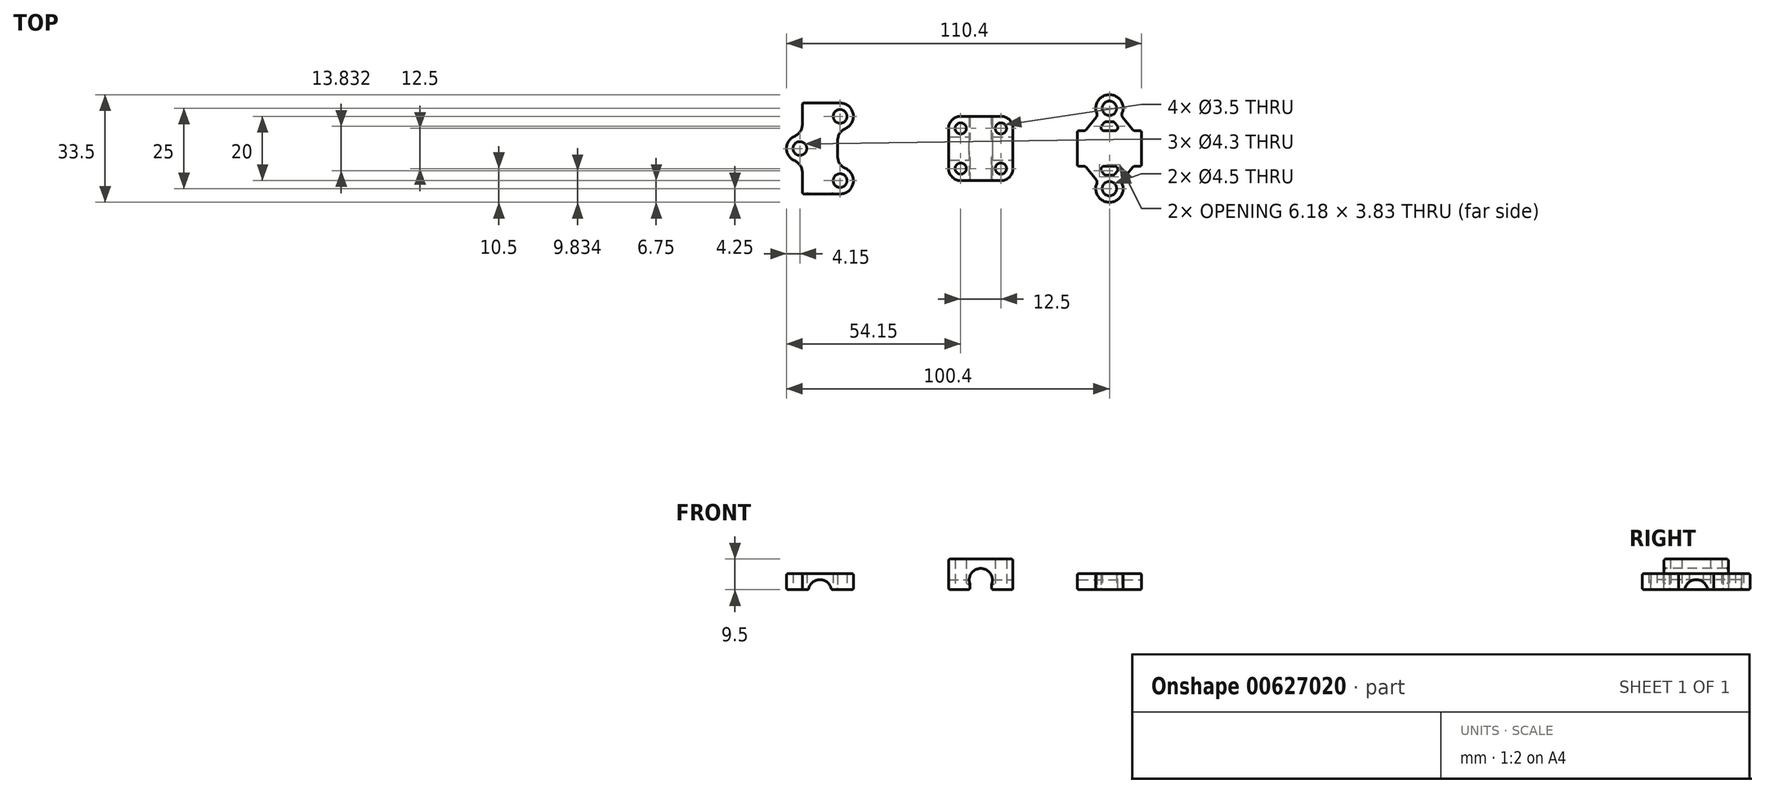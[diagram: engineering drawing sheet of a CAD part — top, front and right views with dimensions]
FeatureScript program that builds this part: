
annotation { "Feature Type Name" : "Feature", "Feature Type Description" : "" }
export const myFeature = defineFeature(function(context is Context, id is Id, definition is map)
    precondition{}
    {
        {
            var Q0;
            Q0=qCreatedBy(makeId("Top.planeOp"),FACE);
            var sketch = newSketch(context, id + "F0", { "sketchPlane" : qUnion([Q0])});
            skLineSegment(sketch, "E0", {"start": v(3.5, 3.7) * mm, "end": v(3.5, 0) * mm, "construction": true});
            skCircle(sketch, "E1", {"center": v(6.25, 6.25) * mm, "radius": 1.75 * mm});
            skLineSegment(sketch, "E2", {"start": v(8.8, 3.5) * mm, "end": v(0, 3.5) * mm, "construction": true});
            skArc(sketch, "E3", {"start": v(10, 6.25) * mm, "mid": v(8.9, 8.9) * mm, "end": v(6.25, 10) * mm});
            skLineSegment(sketch, "E4", {"start": v(6.25, 10) * mm, "end": v(0, 10) * mm});
            skLineSegment(sketch, "E5", {"start": v(10, 6.25) * mm, "end": v(10, 0) * mm});
            skLineSegment(sketch, "E6.MirrorCS", {"start": v(-6.25, 10) * mm, "end": v(0, 10) * mm});
            skArc(sketch, "E7.MirrorCS", {"start": v(-10, 6.25) * mm, "mid": v(-8.9, 8.9) * mm, "end": v(-6.25, 10) * mm});
            skLineSegment(sketch, "E8.MirrorCS", {"start": v(-10, 6.25) * mm, "end": v(-10, 0) * mm});
            skCircle(sketch, "E9.MirrorC", {"center": v(-6.25, 6.25) * mm, "radius": 1.75 * mm});
            skLineSegment(sketch, "E10.MirrorCS", {"start": v(-10, -6.25) * mm, "end": v(-10, 0) * mm});
            skArc(sketch, "E11.MirrorCS", {"start": v(-10, -6.25) * mm, "mid": v(-8.9, -8.9) * mm, "end": v(-6.25, -10) * mm});
            skCircle(sketch, "E12.MirrorC", {"center": v(-6.25, -6.25) * mm, "radius": 1.75 * mm});
            skLineSegment(sketch, "E13.MirrorCS", {"start": v(-6.25, -10) * mm, "end": v(0, -10) * mm});
            skLineSegment(sketch, "E14.MirrorCS", {"start": v(6.25, -10) * mm, "end": v(0, -10) * mm});
            skArc(sketch, "E15.MirrorCS", {"start": v(10, -6.25) * mm, "mid": v(8.9, -8.9) * mm, "end": v(6.25, -10) * mm});
            skCircle(sketch, "E16.MirrorC", {"center": v(6.25, -6.25) * mm, "radius": 1.75 * mm});
            skLineSegment(sketch, "E17.MirrorCS", {"start": v(10, -6.25) * mm, "end": v(10, 0) * mm});
            skSolve(sketch);
        }
        {
            var Q0;
            Q0 = qSketchRegion(id + "F0", true);
            extrude(context, id + "F1", {"entities" : qUnion([Q0]), "depth" : 10 * mm, "offsetDistance" : 25 * mm, "hasSecondDirection" : true, "secondDirectionOppositeDirection" : true, "secondDirectionDepth" : -0.5 * mm});
        }
        {
            var Q0;
            Q0=qCreatedBy(makeId("Front.planeOp"),FACE);
            var sketch = newSketch(context, id + "F2", { "sketchPlane" : qUnion([Q0])});
            skArc(sketch, "E18", {"start": v(3.4, 2.32) * mm, "mid": v(0, 7.1) * mm, "end": v(-3.4, 2.32) * mm});
            skLineSegment(sketch, "E19", {"start": v(-3.4, 2.32) * mm, "end": v(-3.4, 0) * mm});
            skLineSegment(sketch, "E20", {"start": v(-3.4, 0) * mm, "end": v(3.4, 0) * mm});
            skLineSegment(sketch, "E21.MirrorCS", {"start": v(3.4, 2.32) * mm, "end": v(3.4, 0) * mm});
            skSolve(sketch);
        }
        {
            var Q0;
            Q0 = qSketchRegion(id + "F2", true);
            extrude(context, id + "F3", {"entities" : qUnion([Q0]), "operationType" : NewBodyOperationType.REMOVE, "endBound" : BoundingType.SYMMETRIC, "oppositeDirection" : true, "depth" : 25 * mm, "offsetDistance" : 25 * mm});
        }
        {
            var Q0;
            Q0=makeQuery(id+"F3.boolean.opBoolean","INTERSECT",EDGE,{"derivedFrom":[makeQuery(id+"F1.opExtrude","SWEPT_FACE",FACE,{"disambiguationData":[OSD([sQuery(id+"F0.wireOp",EDGE,"E4"),sQuery(id+"F0.wireOp",EDGE,"E6.MirrorCS")])]}),makeQuery(id+"F3.opExtrude","SWEPT_FACE",FACE,{"disambiguationData":[OSD([sQuery(id+"F2.wireOp",EDGE,"E18")])]})]});
            var Q1;
            Q1=makeQuery(id+"F3.boolean.opBoolean","INTERSECT",EDGE,{"derivedFrom":[makeQuery(id+"F1.opExtrude","SWEPT_FACE",FACE,{"disambiguationData":[OSD([sQuery(id+"F0.wireOp",EDGE,"E4"),sQuery(id+"F0.wireOp",EDGE,"E6.MirrorCS")])]}),makeQuery(id+"F3.opExtrude","SWEPT_FACE",FACE,{"disambiguationData":[OSD([sQuery(id+"F2.wireOp",EDGE,"E21.MirrorCS")])]})]});
            var Q2;
            Q2=makeQuery(id+"F3.boolean.opBoolean","INTERSECT",EDGE,{"derivedFrom":[makeQuery(id+"F1.opExtrude","SWEPT_FACE",FACE,{"disambiguationData":[OSD([sQuery(id+"F0.wireOp",EDGE,"E4"),sQuery(id+"F0.wireOp",EDGE,"E6.MirrorCS")])]}),makeQuery(id+"F3.opExtrude","SWEPT_FACE",FACE,{"disambiguationData":[OSD([sQuery(id+"F2.wireOp",EDGE,"E19")])]})]});
            var Q3;
            Q3=makeQuery(id+"F3.boolean.opBoolean","INTERSECT",EDGE,{"derivedFrom":[makeQuery(id+"F1.opExtrude","SWEPT_FACE",FACE,{"disambiguationData":[OSD([sQuery(id+"F0.wireOp",EDGE,"E13.MirrorCS"),sQuery(id+"F0.wireOp",EDGE,"E14.MirrorCS")])]}),makeQuery(id+"F3.opExtrude","SWEPT_FACE",FACE,{"disambiguationData":[OSD([sQuery(id+"F2.wireOp",EDGE,"E18")])]})]});
            var Q4;
            Q4=makeQuery(id+"F3.boolean.opBoolean","INTERSECT",EDGE,{"derivedFrom":[makeQuery(id+"F1.opExtrude","SWEPT_FACE",FACE,{"disambiguationData":[OSD([sQuery(id+"F0.wireOp",EDGE,"E13.MirrorCS"),sQuery(id+"F0.wireOp",EDGE,"E14.MirrorCS")])]}),makeQuery(id+"F3.opExtrude","SWEPT_FACE",FACE,{"disambiguationData":[OSD([sQuery(id+"F2.wireOp",EDGE,"E21.MirrorCS")])]})]});
            var Q5;
            Q5=makeQuery(id+"F3.boolean.opBoolean","INTERSECT",EDGE,{"derivedFrom":[makeQuery(id+"F1.opExtrude","SWEPT_FACE",FACE,{"disambiguationData":[OSD([sQuery(id+"F0.wireOp",EDGE,"E13.MirrorCS"),sQuery(id+"F0.wireOp",EDGE,"E14.MirrorCS")])]}),makeQuery(id+"F3.opExtrude","SWEPT_FACE",FACE,{"disambiguationData":[OSD([sQuery(id+"F2.wireOp",EDGE,"E19")])]})]});
            var Q6;
            Q6=makeQuery(id+"F3.boolean.opBoolean","COPY",EDGE,{"derivedFrom":makeQuery(id+"F3.opExtrude","SWEPT_EDGE",EDGE,{"disambiguationData":[OSD([sQuery(id+"F2.wireOp",EDGE,"E18"),sQuery(id+"F2.wireOp",EDGE,"E21.MirrorCS")])]})});
            var Q7;
            Q7=makeQuery(id+"F3.boolean.opBoolean","COPY",EDGE,{"derivedFrom":makeQuery(id+"F3.opExtrude","SWEPT_EDGE",EDGE,{"disambiguationData":[OSD([sQuery(id+"F2.wireOp",EDGE,"E18"),sQuery(id+"F2.wireOp",EDGE,"E19")])]})});
            var Q8;
            Q8=makeQuery(id+"F1.opExtrude","CAP_EDGE",EDGE,{"disambiguationData":[OSD([sQuery(id+"F0.wireOp",EDGE,"E8.MirrorCS"),sQuery(id+"F0.wireOp",EDGE,"E10.MirrorCS")])],"isStart":true});
            var Q9;
            Q9=makeQuery(id+"F3.boolean.opBoolean","INTERSECT",EDGE,{"derivedFrom":[makeQuery(id+"F1.opExtrude","CAP_FACE",FACE,{"disambiguationData":[OSD([sQuery(id+"F0.wireOp",EDGE,"E1"),sQuery(id+"F0.wireOp",EDGE,"E3"),sQuery(id+"F0.wireOp",EDGE,"E4"),sQuery(id+"F0.wireOp",EDGE,"E5"),sQuery(id+"F0.wireOp",EDGE,"E6.MirrorCS"),sQuery(id+"F0.wireOp",EDGE,"E7.MirrorCS"),sQuery(id+"F0.wireOp",EDGE,"E8.MirrorCS"),sQuery(id+"F0.wireOp",EDGE,"E9.MirrorC"),sQuery(id+"F0.wireOp",EDGE,"E10.MirrorCS"),sQuery(id+"F0.wireOp",EDGE,"E11.MirrorCS"),sQuery(id+"F0.wireOp",EDGE,"E12.MirrorC"),sQuery(id+"F0.wireOp",EDGE,"E13.MirrorCS"),sQuery(id+"F0.wireOp",EDGE,"E14.MirrorCS"),sQuery(id+"F0.wireOp",EDGE,"E15.MirrorCS"),sQuery(id+"F0.wireOp",EDGE,"E16.MirrorC"),sQuery(id+"F0.wireOp",EDGE,"E17.MirrorCS")])],"isStart":true}),makeQuery(id+"F3.opExtrude","SWEPT_FACE",FACE,{"disambiguationData":[OSD([sQuery(id+"F2.wireOp",EDGE,"E19")])]})]});
            var Q10;
            Q10=makeQuery(id+"F1.opExtrude","CAP_EDGE",EDGE,{"disambiguationData":[OSD([sQuery(id+"F0.wireOp",EDGE,"E5"),sQuery(id+"F0.wireOp",EDGE,"E17.MirrorCS")])],"isStart":true});
            var Q11;
            Q11=makeQuery(id+"F3.boolean.opBoolean","INTERSECT",EDGE,{"derivedFrom":[makeQuery(id+"F1.opExtrude","CAP_FACE",FACE,{"disambiguationData":[OSD([sQuery(id+"F0.wireOp",EDGE,"E1"),sQuery(id+"F0.wireOp",EDGE,"E3"),sQuery(id+"F0.wireOp",EDGE,"E4"),sQuery(id+"F0.wireOp",EDGE,"E5"),sQuery(id+"F0.wireOp",EDGE,"E6.MirrorCS"),sQuery(id+"F0.wireOp",EDGE,"E7.MirrorCS"),sQuery(id+"F0.wireOp",EDGE,"E8.MirrorCS"),sQuery(id+"F0.wireOp",EDGE,"E9.MirrorC"),sQuery(id+"F0.wireOp",EDGE,"E10.MirrorCS"),sQuery(id+"F0.wireOp",EDGE,"E11.MirrorCS"),sQuery(id+"F0.wireOp",EDGE,"E12.MirrorC"),sQuery(id+"F0.wireOp",EDGE,"E13.MirrorCS"),sQuery(id+"F0.wireOp",EDGE,"E14.MirrorCS"),sQuery(id+"F0.wireOp",EDGE,"E15.MirrorCS"),sQuery(id+"F0.wireOp",EDGE,"E16.MirrorC"),sQuery(id+"F0.wireOp",EDGE,"E17.MirrorCS")])],"isStart":true}),makeQuery(id+"F3.opExtrude","SWEPT_FACE",FACE,{"disambiguationData":[OSD([sQuery(id+"F2.wireOp",EDGE,"E21.MirrorCS")])]})]});
            var Q12;
            Q12=makeQuery(id+"F1.opExtrude","CAP_EDGE",EDGE,{"disambiguationData":[OSD([sQuery(id+"F0.wireOp",EDGE,"E5"),sQuery(id+"F0.wireOp",EDGE,"E17.MirrorCS")])],"isStart":false});
            fillet(context, id + "F4", {"entities" : qUnion([Q0, Q1, Q2, Q3, Q4, Q5, Q6, Q7, Q8, Q9, Q10, Q11, Q12]), "radius" : 0.5 * mm, "tangentPropagation" : true, "allowEdgeOverflow" : false});
        }
        {
            var Q0;
            Q0=qCreatedBy(makeId("Top.planeOp"),FACE);
            var sketch = newSketch(context, id + "F5", { "sketchPlane" : qUnion([Q0])});
            skCircle(sketch, "E22", {"center": v(40, 12.5) * mm, "radius": 2.25 * mm});
            skArc(sketch, "E23", {"start": v(38.69, 8.46) * mm, "mid": v(40, 8.25) * mm, "end": v(41.31, 8.46) * mm});
            skLineSegment(sketch, "E24.top", {"start": v(30, 5.5) * mm, "end": v(32.48, 5.5) * mm});
            skLineSegment(sketch, "E24.left", {"start": v(30, 0) * mm, "end": v(30, 5.5) * mm});
            skLineSegment(sketch, "E24.right", {"start": v(50, 0) * mm, "end": v(50, 5.5) * mm});
            skLineSegment(sketch, "E25", {"start": v(30, 0) * mm, "end": v(40, 12.5) * mm, "construction": true});
            skLineSegment(sketch, "E26", {"start": v(32.48, 5.5) * mm, "end": v(36.34, 10.33) * mm});
            skLineSegment(sketch, "E27", {"start": v(36.32, 5.5) * mm, "end": v(38.69, 8.46) * mm});
            skLineSegment(sketch, "E28", {"start": v(40, 11.56) * mm, "end": v(40, 10.25) * mm, "construction": true});
            skLineSegment(sketch, "E29.MirrorCS", {"start": v(43.68, 5.5) * mm, "end": v(41.31, 8.46) * mm});
            skLineSegment(sketch, "E30.MirrorCS", {"start": v(47.52, 5.5) * mm, "end": v(43.66, 10.33) * mm});
            skLineSegment(sketch, "E31.trimOffspring", {"start": v(36.32, 5.5) * mm, "end": v(43.68, 5.5) * mm});
            skArc(sketch, "E32.trimOffspring", {"start": v(43.66, 10.33) * mm, "mid": v(40, 16.75) * mm, "end": v(36.34, 10.33) * mm});
            skLineSegment(sketch, "E33.trimOffspring", {"start": v(47.52, 5.5) * mm, "end": v(50, 5.5) * mm});
            skPoint(sketch, "E34.orphan", {"position": v(40, 0) * mm});
            skLineSegment(sketch, "E35.MirrorCS", {"start": v(30, 0) * mm, "end": v(30, -5.5) * mm});
            skLineSegment(sketch, "E36.MirrorCS", {"start": v(30, -5.5) * mm, "end": v(32.48, -5.5) * mm});
            skLineSegment(sketch, "E37.MirrorCS", {"start": v(32.48, -5.5) * mm, "end": v(36.34, -10.33) * mm});
            skArc(sketch, "E38.MirrorCS", {"start": v(43.66, -10.33) * mm, "mid": v(40, -16.75) * mm, "end": v(36.34, -10.33) * mm});
            skLineSegment(sketch, "E39.MirrorCS", {"start": v(47.52, -5.5) * mm, "end": v(43.66, -10.33) * mm});
            skLineSegment(sketch, "E40.MirrorCS", {"start": v(47.52, -5.5) * mm, "end": v(50, -5.5) * mm});
            skLineSegment(sketch, "E41.MirrorCS", {"start": v(50, 0) * mm, "end": v(50, -5.5) * mm});
            skCircle(sketch, "E42.MirrorC", {"center": v(40, -12.5) * mm, "radius": 2.25 * mm});
            skArc(sketch, "E43.MirrorCS", {"start": v(38.69, -8.46) * mm, "mid": v(40, -8.25) * mm, "end": v(41.31, -8.46) * mm});
            skLineSegment(sketch, "E44.MirrorCS", {"start": v(36.32, -5.5) * mm, "end": v(38.69, -8.46) * mm});
            skLineSegment(sketch, "E45.MirrorCS", {"start": v(36.32, -5.5) * mm, "end": v(43.68, -5.5) * mm});
            skLineSegment(sketch, "E46.MirrorCS", {"start": v(43.68, -5.5) * mm, "end": v(41.31, -8.46) * mm});
            skSolve(sketch);
        }
        {
            var Q0;
            Q0 = qSketchRegion(id + "F5", true);
            extrude(context, id + "F6", {"entities" : qUnion([Q0]), "depth" : 5.5 * mm, "offsetDistance" : 25 * mm, "hasSecondDirection" : true, "secondDirectionOppositeDirection" : true, "secondDirectionDepth" : -0.5 * mm});
        }
        {
            var Q0;
            Q0=makeQuery(id+"F6.opExtrude","SWEPT_FACE",FACE,{"disambiguationData":[OSD([sQuery(id+"F5.wireOp",EDGE,"E24.right"),sQuery(id+"F5.wireOp",EDGE,"E41.MirrorCS")])]});
            var sketch = newSketch(context, id + "F7", { "sketchPlane" : qUnion([Q0])});
            skCircle(sketch, "E47", {"center": v(0, 0) * mm, "radius": 3.6 * mm});
            skSolve(sketch);
        }
        {
            var Q0;
            Q0 = qSketchRegion(id + "F7", true);
            extrude(context, id + "F8", {"entities" : qUnion([Q0]), "operationType" : NewBodyOperationType.REMOVE, "endBound" : BoundingType.THROUGH_ALL, "oppositeDirection" : true, "depth" : 25 * mm, "offsetDistance" : 25 * mm});
        }
        {
            var Q0;
            Q0=makeQuery(id+"F6.opExtrude","SWEPT_EDGE",EDGE,{"disambiguationData":[OSD([sQuery(id+"F5.wireOp",EDGE,"E30.MirrorCS"),sQuery(id+"F5.wireOp",EDGE,"E32.trimOffspring")])]});
            var Q1;
            Q1=makeQuery(id+"F6.opExtrude","SWEPT_EDGE",EDGE,{"disambiguationData":[OSD([sQuery(id+"F5.wireOp",EDGE,"E30.MirrorCS"),sQuery(id+"F5.wireOp",EDGE,"E33.trimOffspring")])]});
            var Q2;
            Q2=makeQuery(id+"F6.opExtrude","SWEPT_EDGE",EDGE,{"disambiguationData":[OSD([sQuery(id+"F5.wireOp",EDGE,"E26"),sQuery(id+"F5.wireOp",EDGE,"E32.trimOffspring")])]});
            var Q3;
            Q3=makeQuery(id+"F6.opExtrude","SWEPT_EDGE",EDGE,{"disambiguationData":[OSD([sQuery(id+"F5.wireOp",EDGE,"E24.top"),sQuery(id+"F5.wireOp",EDGE,"E26")])]});
            var Q4;
            Q4=makeQuery(id+"F6.opExtrude","SWEPT_EDGE",EDGE,{"disambiguationData":[OSD([sQuery(id+"F5.wireOp",EDGE,"E23"),sQuery(id+"F5.wireOp",EDGE,"E27")])]});
            var Q5;
            Q5=makeQuery(id+"F6.opExtrude","SWEPT_EDGE",EDGE,{"disambiguationData":[OSD([sQuery(id+"F5.wireOp",EDGE,"E23"),sQuery(id+"F5.wireOp",EDGE,"E29.MirrorCS")])]});
            var Q6;
            Q6=makeQuery(id+"F6.opExtrude","SWEPT_EDGE",EDGE,{"disambiguationData":[OSD([sQuery(id+"F5.wireOp",EDGE,"E27"),sQuery(id+"F5.wireOp",EDGE,"E31.trimOffspring")])]});
            var Q7;
            Q7=makeQuery(id+"F6.opExtrude","SWEPT_EDGE",EDGE,{"disambiguationData":[OSD([sQuery(id+"F5.wireOp",EDGE,"E29.MirrorCS"),sQuery(id+"F5.wireOp",EDGE,"E31.trimOffspring")])]});
            var Q8;
            Q8=makeQuery(id+"F6.opExtrude","SWEPT_EDGE",EDGE,{"disambiguationData":[OSD([sQuery(id+"F5.wireOp",EDGE,"E43.MirrorCS"),sQuery(id+"F5.wireOp",EDGE,"E46.MirrorCS")])]});
            var Q9;
            Q9=makeQuery(id+"F6.opExtrude","SWEPT_EDGE",EDGE,{"disambiguationData":[OSD([sQuery(id+"F5.wireOp",EDGE,"E43.MirrorCS"),sQuery(id+"F5.wireOp",EDGE,"E44.MirrorCS")])]});
            var Q10;
            Q10=makeQuery(id+"F6.opExtrude","SWEPT_EDGE",EDGE,{"disambiguationData":[OSD([sQuery(id+"F5.wireOp",EDGE,"E45.MirrorCS"),sQuery(id+"F5.wireOp",EDGE,"E46.MirrorCS")])]});
            var Q11;
            Q11=makeQuery(id+"F6.opExtrude","SWEPT_EDGE",EDGE,{"disambiguationData":[OSD([sQuery(id+"F5.wireOp",EDGE,"E44.MirrorCS"),sQuery(id+"F5.wireOp",EDGE,"E45.MirrorCS")])]});
            var Q12;
            Q12=makeQuery(id+"F6.opExtrude","SWEPT_EDGE",EDGE,{"disambiguationData":[OSD([sQuery(id+"F5.wireOp",EDGE,"E38.MirrorCS"),sQuery(id+"F5.wireOp",EDGE,"E39.MirrorCS")])]});
            var Q13;
            Q13=makeQuery(id+"F6.opExtrude","SWEPT_EDGE",EDGE,{"disambiguationData":[OSD([sQuery(id+"F5.wireOp",EDGE,"E36.MirrorCS"),sQuery(id+"F5.wireOp",EDGE,"E37.MirrorCS")])]});
            var Q14;
            Q14=makeQuery(id+"F6.opExtrude","SWEPT_EDGE",EDGE,{"disambiguationData":[OSD([sQuery(id+"F5.wireOp",EDGE,"E37.MirrorCS"),sQuery(id+"F5.wireOp",EDGE,"E38.MirrorCS")])]});
            var Q15;
            Q15=makeQuery(id+"F6.opExtrude","SWEPT_EDGE",EDGE,{"disambiguationData":[OSD([sQuery(id+"F5.wireOp",EDGE,"E39.MirrorCS"),sQuery(id+"F5.wireOp",EDGE,"E40.MirrorCS")])]});
            fillet(context, id + "F9", {"entities" : qUnion([Q0, Q1, Q2, Q3, Q4, Q5, Q6, Q7, Q8, Q9, Q10, Q11, Q12, Q13, Q14, Q15]), "radius" : 1 * mm, "tangentPropagation" : true, "allowEdgeOverflow" : false});
        }
        {
            var Q0;
            Q0=makeQuery(id+"F6.opExtrude","CAP_EDGE",EDGE,{"disambiguationData":[OSD([sQuery(id+"F5.wireOp",EDGE,"E38.MirrorCS")])],"isStart":true});
            var Q1;
            Q1=makeQuery(id+"F6.opExtrude","CAP_EDGE",EDGE,{"disambiguationData":[OSD([sQuery(id+"F5.wireOp",EDGE,"E44.MirrorCS")])],"isStart":true});
            var Q2;
            Q2=makeQuery(id+"F8.boolean.opBoolean","INTERSECT",EDGE,{"disambiguationData":[OD(1.0)],"derivedFrom":[makeQuery(id+"F6.opExtrude","CAP_FACE",FACE,{"disambiguationData":[OSD([sQuery(id+"F5.wireOp",EDGE,"E22"),sQuery(id+"F5.wireOp",EDGE,"E23"),sQuery(id+"F5.wireOp",EDGE,"E24.top"),sQuery(id+"F5.wireOp",EDGE,"E24.left"),sQuery(id+"F5.wireOp",EDGE,"E24.right"),sQuery(id+"F5.wireOp",EDGE,"E26"),sQuery(id+"F5.wireOp",EDGE,"E27"),sQuery(id+"F5.wireOp",EDGE,"E29.MirrorCS"),sQuery(id+"F5.wireOp",EDGE,"E30.MirrorCS"),sQuery(id+"F5.wireOp",EDGE,"E31.trimOffspring"),sQuery(id+"F5.wireOp",EDGE,"E32.trimOffspring"),sQuery(id+"F5.wireOp",EDGE,"E33.trimOffspring"),sQuery(id+"F5.wireOp",EDGE,"E35.MirrorCS"),sQuery(id+"F5.wireOp",EDGE,"E36.MirrorCS"),sQuery(id+"F5.wireOp",EDGE,"E37.MirrorCS"),sQuery(id+"F5.wireOp",EDGE,"E38.MirrorCS"),sQuery(id+"F5.wireOp",EDGE,"E39.MirrorCS"),sQuery(id+"F5.wireOp",EDGE,"E40.MirrorCS"),sQuery(id+"F5.wireOp",EDGE,"E41.MirrorCS"),sQuery(id+"F5.wireOp",EDGE,"E42.MirrorC"),sQuery(id+"F5.wireOp",EDGE,"E43.MirrorCS"),sQuery(id+"F5.wireOp",EDGE,"E44.MirrorCS"),sQuery(id+"F5.wireOp",EDGE,"E45.MirrorCS"),sQuery(id+"F5.wireOp",EDGE,"E46.MirrorCS")])],"isStart":true}),makeQuery(id+"F8.opExtrude","SWEPT_FACE",FACE,{"disambiguationData":[OSD([sQuery(id+"F7.wireOp",EDGE,"E47")])]})]});
            var Q3;
            Q3=makeQuery(id+"F8.boolean.opBoolean","INTERSECT",EDGE,{"disambiguationData":[OD(0.0)],"derivedFrom":[makeQuery(id+"F6.opExtrude","CAP_FACE",FACE,{"disambiguationData":[OSD([sQuery(id+"F5.wireOp",EDGE,"E22"),sQuery(id+"F5.wireOp",EDGE,"E23"),sQuery(id+"F5.wireOp",EDGE,"E24.top"),sQuery(id+"F5.wireOp",EDGE,"E24.left"),sQuery(id+"F5.wireOp",EDGE,"E24.right"),sQuery(id+"F5.wireOp",EDGE,"E26"),sQuery(id+"F5.wireOp",EDGE,"E27"),sQuery(id+"F5.wireOp",EDGE,"E29.MirrorCS"),sQuery(id+"F5.wireOp",EDGE,"E30.MirrorCS"),sQuery(id+"F5.wireOp",EDGE,"E31.trimOffspring"),sQuery(id+"F5.wireOp",EDGE,"E32.trimOffspring"),sQuery(id+"F5.wireOp",EDGE,"E33.trimOffspring"),sQuery(id+"F5.wireOp",EDGE,"E35.MirrorCS"),sQuery(id+"F5.wireOp",EDGE,"E36.MirrorCS"),sQuery(id+"F5.wireOp",EDGE,"E37.MirrorCS"),sQuery(id+"F5.wireOp",EDGE,"E38.MirrorCS"),sQuery(id+"F5.wireOp",EDGE,"E39.MirrorCS"),sQuery(id+"F5.wireOp",EDGE,"E40.MirrorCS"),sQuery(id+"F5.wireOp",EDGE,"E41.MirrorCS"),sQuery(id+"F5.wireOp",EDGE,"E42.MirrorC"),sQuery(id+"F5.wireOp",EDGE,"E43.MirrorCS"),sQuery(id+"F5.wireOp",EDGE,"E44.MirrorCS"),sQuery(id+"F5.wireOp",EDGE,"E45.MirrorCS"),sQuery(id+"F5.wireOp",EDGE,"E46.MirrorCS")])],"isStart":true}),makeQuery(id+"F8.opExtrude","SWEPT_FACE",FACE,{"disambiguationData":[OSD([sQuery(id+"F7.wireOp",EDGE,"E47")])]})]});
            var Q4;
            Q4=makeQuery(id+"F6.opExtrude","CAP_EDGE",EDGE,{"disambiguationData":[OSD([sQuery(id+"F5.wireOp",EDGE,"E27")])],"isStart":true});
            var Q5;
            Q5=makeQuery(id+"F6.opExtrude","CAP_EDGE",EDGE,{"disambiguationData":[OSD([sQuery(id+"F5.wireOp",EDGE,"E26")])],"isStart":true});
            var Q6;
            Q6=makeQuery(id+"F6.opExtrude","CAP_EDGE",EDGE,{"disambiguationData":[OSD([sQuery(id+"F5.wireOp",EDGE,"E38.MirrorCS")])],"isStart":false});
            var Q7;
            Q7=makeQuery(id+"F6.opExtrude","CAP_EDGE",EDGE,{"disambiguationData":[OSD([sQuery(id+"F5.wireOp",EDGE,"E45.MirrorCS")])],"isStart":false});
            var Q8;
            Q8=makeQuery(id+"F6.opExtrude","CAP_EDGE",EDGE,{"disambiguationData":[OSD([sQuery(id+"F5.wireOp",EDGE,"E31.trimOffspring")])],"isStart":false});
            var Q9;
            Q9=makeQuery(id+"F6.opExtrude","CAP_EDGE",EDGE,{"disambiguationData":[OSD([sQuery(id+"F5.wireOp",EDGE,"E30.MirrorCS")])],"isStart":false});
            var Q10;
            Q10=makeQuery(id+"F6.opExtrude","SWEPT_FACE",FACE,{"disambiguationData":[OSD([sQuery(id+"F5.wireOp",EDGE,"E24.right"),sQuery(id+"F5.wireOp",EDGE,"E41.MirrorCS")])]});
            var Q11;
            Q11=makeQuery(id+"F6.opExtrude","SWEPT_FACE",FACE,{"disambiguationData":[OSD([sQuery(id+"F5.wireOp",EDGE,"E24.left"),sQuery(id+"F5.wireOp",EDGE,"E35.MirrorCS")])]});
            fillet(context, id + "F10", {"entities" : qUnion([Q0, Q1, Q2, Q3, Q4, Q5, Q6, Q7, Q8, Q9, Q10, Q11]), "radius" : 0.5 * mm, "tangentPropagation" : true, "allowEdgeOverflow" : false});
        }
        {
            var Q0;
            Q0=qCreatedBy(makeId("Top.planeOp"),FACE);
            var sketch = newSketch(context, id + "F11", { "sketchPlane" : qUnion([Q0])});
            skCircle(sketch, "E48", {"center": v(-43.75, 10) * mm, "radius": 2.15 * mm});
            skCircle(sketch, "E49", {"center": v(-43.75, -10) * mm, "radius": 2.15 * mm});
            skCircle(sketch, "E50", {"center": v(-56.25, 0) * mm, "radius": 2.15 * mm});
            skArc(sketch, "E51", {"start": v(-44.5, 5.92) * mm, "mid": v(-39.62, 9.62) * mm, "end": v(-43.75, 14.15) * mm});
            skArc(sketch, "E52", {"start": v(-43.75, -14.15) * mm, "mid": v(-39.62, -9.62) * mm, "end": v(-44.5, -5.92) * mm});
            skArc(sketch, "E53", {"start": v(-55.5, 4.08) * mm, "mid": v(-60.4, 0) * mm, "end": v(-55.5, -4.08) * mm});
            skLineSegment(sketch, "E54", {"start": v(-50, 10) * mm, "end": v(-50, -10) * mm, "construction": true});
            skLineSegment(sketch, "E55", {"start": v(-55.5, 14.15) * mm, "end": v(-43.75, 14.15) * mm});
            skLineSegment(sketch, "E56", {"start": v(-55.5, 14.15) * mm, "end": v(-55.5, 4.08) * mm});
            skLineSegment(sketch, "E57", {"start": v(-44.5, 5.92) * mm, "end": v(-44.5, -5.92) * mm});
            skLineSegment(sketch, "E58.MirrorCS", {"start": v(-55.5, -14.15) * mm, "end": v(-55.5, -4.08) * mm});
            skLineSegment(sketch, "E59", {"start": v(-55.5, -14.15) * mm, "end": v(-43.75, -14.15) * mm});
            skSolve(sketch);
        }
        {
            var Q0;
            Q0=makeQuery(id+"F11.imprint","IMPRINT",FACE,{"disambiguationData":[TD([[makeQuery(id+"F11.imprint","IMPRINT",EDGE,{"derivedFrom":sQuery(id+"F11.wireOp",EDGE,"E48")}),-1.0]])]});
            extrude(context, id + "F12", {"entities" : qUnion([Q0]), "depth" : 5.5 * mm, "offsetDistance" : 25 * mm, "hasSecondDirection" : true, "secondDirectionOppositeDirection" : true, "secondDirectionDepth" : -0.5 * mm});
        }
        {
            var Q0;
            Q0=makeQuery(id+"F12.opExtrude","SWEPT_EDGE",EDGE,{"disambiguationData":[OSD([sQuery(id+"F11.wireOp",EDGE,"E53"),sQuery(id+"F11.wireOp",EDGE,"E58.MirrorCS")])]});
            var Q1;
            Q1=makeQuery(id+"F12.opExtrude","SWEPT_EDGE",EDGE,{"disambiguationData":[OSD([sQuery(id+"F11.wireOp",EDGE,"E53"),sQuery(id+"F11.wireOp",EDGE,"E56")])]});
            var Q2;
            Q2=makeQuery(id+"F12.opExtrude","SWEPT_EDGE",EDGE,{"disambiguationData":[OSD([sQuery(id+"F11.wireOp",EDGE,"E51"),sQuery(id+"F11.wireOp",EDGE,"E57")])]});
            var Q3;
            Q3=makeQuery(id+"F12.opExtrude","SWEPT_EDGE",EDGE,{"disambiguationData":[OSD([sQuery(id+"F11.wireOp",EDGE,"E52"),sQuery(id+"F11.wireOp",EDGE,"E57")])]});
            fillet(context, id + "F13", {"entities" : qUnion([Q0, Q1, Q2, Q3]), "radius" : 4 * mm, "tangentPropagation" : true, "allowEdgeOverflow" : false});
        }
        {
            var Q0;
            Q0=makeQuery(id+"F12.opExtrude","SWEPT_FACE",FACE,{"disambiguationData":[OSD([sQuery(id+"F11.wireOp",EDGE,"E59")])]});
            var sketch = newSketch(context, id + "F14", { "sketchPlane" : qUnion([Q0])});
            skCircle(sketch, "E60", {"center": v(-50, 0) * mm, "radius": 3.6 * mm});
            skSolve(sketch);
        }
        {
            var Q0;
            Q0 = qSketchRegion(id + "F14", true);
            extrude(context, id + "F15", {"entities" : qUnion([Q0]), "operationType" : NewBodyOperationType.REMOVE, "endBound" : BoundingType.THROUGH_ALL, "oppositeDirection" : true, "depth" : 25 * mm, "offsetDistance" : 25 * mm});
        }
        {
            var Q0;
            Q0=makeQuery(id+"F15.boolean.opBoolean","INTERSECT",EDGE,{"disambiguationData":[OD(1.0)],"derivedFrom":[makeQuery(id+"F12.opExtrude","CAP_FACE",FACE,{"disambiguationData":[OSD([sQuery(id+"F11.wireOp",EDGE,"E48"),sQuery(id+"F11.wireOp",EDGE,"E49"),sQuery(id+"F11.wireOp",EDGE,"E50"),sQuery(id+"F11.wireOp",EDGE,"E51"),sQuery(id+"F11.wireOp",EDGE,"E52"),sQuery(id+"F11.wireOp",EDGE,"E53"),sQuery(id+"F11.wireOp",EDGE,"E55"),sQuery(id+"F11.wireOp",EDGE,"E56"),sQuery(id+"F11.wireOp",EDGE,"E57"),sQuery(id+"F11.wireOp",EDGE,"E58.MirrorCS"),sQuery(id+"F11.wireOp",EDGE,"E59")])],"isStart":true}),makeQuery(id+"F15.opExtrude","SWEPT_FACE",FACE,{"disambiguationData":[OSD([sQuery(id+"F14.wireOp",EDGE,"E60")])]})]});
            var Q1;
            Q1=makeQuery(id+"F15.boolean.opBoolean","INTERSECT",EDGE,{"disambiguationData":[OD(0.0)],"derivedFrom":[makeQuery(id+"F12.opExtrude","CAP_FACE",FACE,{"disambiguationData":[OSD([sQuery(id+"F11.wireOp",EDGE,"E48"),sQuery(id+"F11.wireOp",EDGE,"E49"),sQuery(id+"F11.wireOp",EDGE,"E50"),sQuery(id+"F11.wireOp",EDGE,"E51"),sQuery(id+"F11.wireOp",EDGE,"E52"),sQuery(id+"F11.wireOp",EDGE,"E53"),sQuery(id+"F11.wireOp",EDGE,"E55"),sQuery(id+"F11.wireOp",EDGE,"E56"),sQuery(id+"F11.wireOp",EDGE,"E57"),sQuery(id+"F11.wireOp",EDGE,"E58.MirrorCS"),sQuery(id+"F11.wireOp",EDGE,"E59")])],"isStart":true}),makeQuery(id+"F15.opExtrude","SWEPT_FACE",FACE,{"disambiguationData":[OSD([sQuery(id+"F14.wireOp",EDGE,"E60")])]})]});
            var Q2;
            Q2=makeQuery(id+"F12.opExtrude","SWEPT_EDGE",EDGE,{"disambiguationData":[OSD([sQuery(id+"F11.wireOp",EDGE,"E58.MirrorCS"),sQuery(id+"F11.wireOp",EDGE,"E59")])]});
            var Q3;
            Q3=makeQuery(id+"F12.opExtrude","SWEPT_EDGE",EDGE,{"disambiguationData":[OSD([sQuery(id+"F11.wireOp",EDGE,"E55"),sQuery(id+"F11.wireOp",EDGE,"E56")])]});
            var Q4;
            Q4=makeQuery(id+"F12.opExtrude","CAP_EDGE",EDGE,{"disambiguationData":[OSD([sQuery(id+"F11.wireOp",EDGE,"E53")])],"isStart":true});
            var Q5;
            {var subQ0=sQuery(id+"F11.wireOp",EDGE,"E57");var subQ1=sQuery(id+"F11.wireOp",EDGE,"E52");Q5=makeQuery(id+"F13.opFillet","BLEND_EDGE",EDGE,{"blendedFrom":[makeQuery(id+"F12.opExtrude","SWEPT_EDGE",EDGE,{"disambiguationData":[OSD([subQ1,subQ0])]}),makeQuery(id+"F12.opExtrude","CAP_FACE",FACE,{"disambiguationData":[OSD([sQuery(id+"F11.wireOp",EDGE,"E48"),sQuery(id+"F11.wireOp",EDGE,"E49"),sQuery(id+"F11.wireOp",EDGE,"E50"),sQuery(id+"F11.wireOp",EDGE,"E51"),subQ1,sQuery(id+"F11.wireOp",EDGE,"E53"),sQuery(id+"F11.wireOp",EDGE,"E55"),sQuery(id+"F11.wireOp",EDGE,"E56"),subQ0,sQuery(id+"F11.wireOp",EDGE,"E58.MirrorCS"),sQuery(id+"F11.wireOp",EDGE,"E59")])],"isStart":true})],"blendedInto":[makeQuery(id+"F12.opExtrude","CAP_FACE",FACE,{"disambiguationData":[OSD([sQuery(id+"F11.wireOp",EDGE,"E48"),sQuery(id+"F11.wireOp",EDGE,"E49"),sQuery(id+"F11.wireOp",EDGE,"E50"),sQuery(id+"F11.wireOp",EDGE,"E51"),subQ1,sQuery(id+"F11.wireOp",EDGE,"E53"),sQuery(id+"F11.wireOp",EDGE,"E55"),sQuery(id+"F11.wireOp",EDGE,"E56"),subQ0,sQuery(id+"F11.wireOp",EDGE,"E58.MirrorCS"),sQuery(id+"F11.wireOp",EDGE,"E59")])],"isStart":true})]});}
            var Q6;
            {var subQ0=sQuery(id+"F11.wireOp",EDGE,"E56");var subQ1=sQuery(id+"F11.wireOp",EDGE,"E55");Q6=makeQuery(id+"F15.boolean.opBoolean","SPLIT",EDGE,{"disambiguationData":[TD([makeQuery(id+"F12.opExtrude","SWEPT_FACE",FACE,{"disambiguationData":[OSD([subQ0])]})])],"derivedFrom":makeQuery(id+"F12.opExtrude","CAP_EDGE",EDGE,{"disambiguationData":[OSD([subQ1])],"isStart":true})});}
            var Q7;
            {var subQ0=sQuery(id+"F11.wireOp",EDGE,"E59");var subQ1=sQuery(id+"F11.wireOp",EDGE,"E58.MirrorCS");Q7=makeQuery(id+"F15.boolean.opBoolean","SPLIT",EDGE,{"disambiguationData":[TD([makeQuery(id+"F12.opExtrude","SWEPT_FACE",FACE,{"disambiguationData":[OSD([subQ1])]})])],"derivedFrom":makeQuery(id+"F12.opExtrude","CAP_EDGE",EDGE,{"disambiguationData":[OSD([subQ0])],"isStart":true})});}
            var Q8;
            Q8=makeQuery(id+"F15.boolean.opBoolean","INTERSECT",EDGE,{"derivedFrom":[makeQuery(id+"F12.opExtrude","SWEPT_FACE",FACE,{"disambiguationData":[OSD([sQuery(id+"F11.wireOp",EDGE,"E55")])]}),makeQuery(id+"F15.opExtrude","SWEPT_FACE",FACE,{"disambiguationData":[OSD([sQuery(id+"F14.wireOp",EDGE,"E60")])]})]});
            var Q9;
            Q9=makeQuery(id+"F15.boolean.opBoolean","COPY",EDGE,{"derivedFrom":makeQuery(id+"F15.opExtrude","CAP_EDGE",EDGE,{"disambiguationData":[OSD([sQuery(id+"F14.wireOp",EDGE,"E60")])],"isStart":true})});
            var Q10;
            Q10=makeQuery(id+"F12.opExtrude","CAP_EDGE",EDGE,{"disambiguationData":[OSD([sQuery(id+"F11.wireOp",EDGE,"E51")])],"isStart":false});
            var Q11;
            {var subQ0=sQuery(id+"F11.wireOp",EDGE,"E58.MirrorCS");var subQ1=sQuery(id+"F11.wireOp",EDGE,"E53");Q11=makeQuery(id+"F13.opFillet","BLEND_EDGE",EDGE,{"blendedFrom":[makeQuery(id+"F12.opExtrude","SWEPT_EDGE",EDGE,{"disambiguationData":[OSD([subQ1,subQ0])]}),makeQuery(id+"F12.opExtrude","CAP_FACE",FACE,{"disambiguationData":[OSD([sQuery(id+"F11.wireOp",EDGE,"E48"),sQuery(id+"F11.wireOp",EDGE,"E49"),sQuery(id+"F11.wireOp",EDGE,"E50"),sQuery(id+"F11.wireOp",EDGE,"E51"),sQuery(id+"F11.wireOp",EDGE,"E52"),subQ1,sQuery(id+"F11.wireOp",EDGE,"E55"),sQuery(id+"F11.wireOp",EDGE,"E56"),sQuery(id+"F11.wireOp",EDGE,"E57"),subQ0,sQuery(id+"F11.wireOp",EDGE,"E59")])],"isStart":false})],"blendedInto":[makeQuery(id+"F12.opExtrude","CAP_FACE",FACE,{"disambiguationData":[OSD([sQuery(id+"F11.wireOp",EDGE,"E48"),sQuery(id+"F11.wireOp",EDGE,"E49"),sQuery(id+"F11.wireOp",EDGE,"E50"),sQuery(id+"F11.wireOp",EDGE,"E51"),sQuery(id+"F11.wireOp",EDGE,"E52"),subQ1,sQuery(id+"F11.wireOp",EDGE,"E55"),sQuery(id+"F11.wireOp",EDGE,"E56"),sQuery(id+"F11.wireOp",EDGE,"E57"),subQ0,sQuery(id+"F11.wireOp",EDGE,"E59")])],"isStart":false})]});}
            fillet(context, id + "F16", {"entities" : qUnion([Q0, Q1, Q2, Q3, Q4, Q5, Q6, Q7, Q8, Q9, Q10, Q11]), "radius" : 0.5 * mm, "tangentPropagation" : true, "allowEdgeOverflow" : false});
        }
    });
